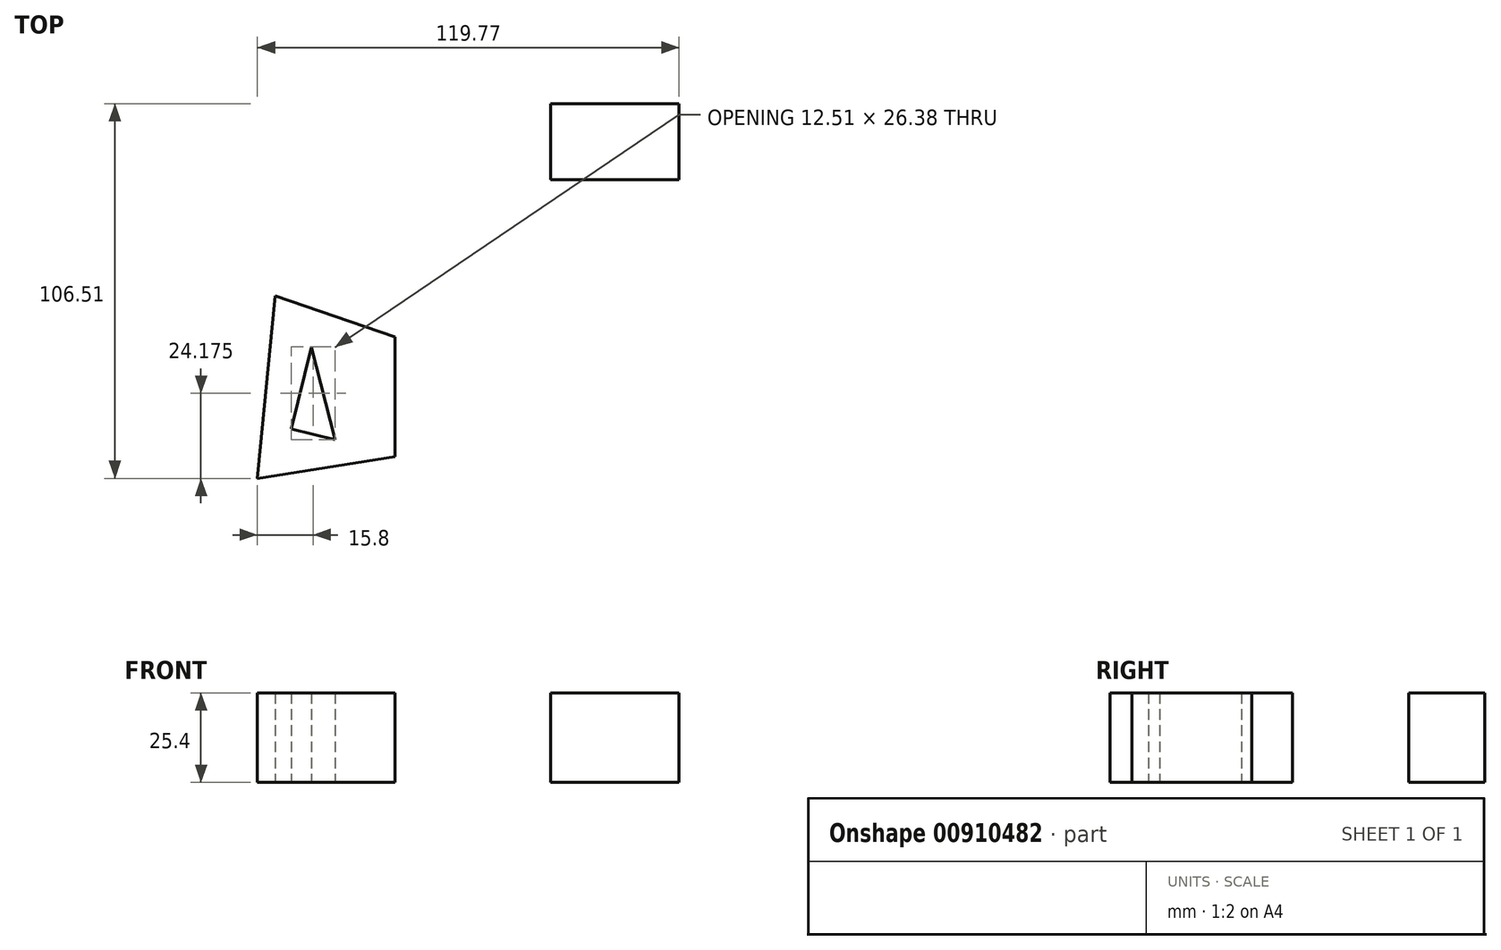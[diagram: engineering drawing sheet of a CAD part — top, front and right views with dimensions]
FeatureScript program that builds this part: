
annotation { "Feature Type Name" : "Feature", "Feature Type Description" : "" }
export const myFeature = defineFeature(function(context is Context, id is Id, definition is map)
    precondition{}
    {
        {
            var Q0;
            Q0=qCreatedBy(makeId("Top.planeOp"),FACE);
            var sketch = newSketch(context, id + "F0", { "sketchPlane" : qUnion([Q0])});
            skCircle(sketch, "E0", {"center": v(-62.28, 52.52) * mm, "radius": 11.18 * mm});
            skLineSegment(sketch, "E1.bottom", {"start": v(23.25, 37.16) * mm, "end": v(59.79, 37.16) * mm});
            skLineSegment(sketch, "E1.top", {"start": v(23.25, 15.57) * mm, "end": v(59.79, 15.57) * mm});
            skLineSegment(sketch, "E1.left", {"start": v(23.25, 37.16) * mm, "end": v(23.25, 15.57) * mm});
            skLineSegment(sketch, "E1.right", {"start": v(59.79, 37.16) * mm, "end": v(59.79, 15.57) * mm});
            skLineSegment(sketch, "E2", {"start": v(-55, -17.45) * mm, "end": v(-20.95, -29.08) * mm});
            skLineSegment(sketch, "E3", {"start": v(-20.95, -29.08) * mm, "end": v(-20.95, -63.13) * mm});
            skLineSegment(sketch, "E4", {"start": v(-20.95, -63.13) * mm, "end": v(-59.98, -69.35) * mm});
            skLineSegment(sketch, "E5", {"start": v(-59.98, -69.35) * mm, "end": v(-55, -17.45) * mm});
            skLineSegment(sketch, "E6", {"start": v(-44.62, -31.99) * mm, "end": v(-50.43, -55.24) * mm});
            skLineSegment(sketch, "E7", {"start": v(-50.43, -55.24) * mm, "end": v(-37.93, -58.36) * mm});
            skLineSegment(sketch, "E8", {"start": v(-37.93, -58.36) * mm, "end": v(-44.62, -31.99) * mm});
            skLineSegment(sketch, "E9", {"start": v(-82.91, 71.7) * mm, "end": v(-82.91, 30.26) * mm, "construction": true});
            skSolve(sketch);
        }
        {
            var Q0;
            Q0=makeQuery(id+"F0.imprint","IMPRINT",FACE,{"disambiguationData":[TD([[makeQuery(id+"F0.imprint","IMPRINT",EDGE,{"derivedFrom":sQuery(id+"F0.wireOp",EDGE,"E2")}),-1.0]])]});
            extrude(context, id + "F1", {"entities" : qUnion([Q0]), "depth" : 25.4 * mm, "offsetDistance" : 25.4 * mm});
        }
        {
            var Q0;
            Q0=sQuery(id+"F0.wireOp",EDGE,"E0");
            extrude(context, id + "F2", {"bodyType" : ToolBodyType.SURFACE, "surfaceEntities" : qUnion([Q0]), "depth" : 25.4 * mm, "offsetDistance" : 25.4 * mm});
        }
        {
            var Q0;
            Q0=makeQuery(id+"F0.imprint","IMPRINT",FACE,{"disambiguationData":[TD([[makeQuery(id+"F0.imprint","IMPRINT",EDGE,{"derivedFrom":sQuery(id+"F0.wireOp",EDGE,"E1.bottom")}),-1.0]])]});
            extrude(context, id + "F3", {"entities" : qUnion([Q0]), "depth" : 25.4 * mm, "offsetDistance" : 25.4 * mm});
        }
    });
